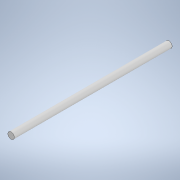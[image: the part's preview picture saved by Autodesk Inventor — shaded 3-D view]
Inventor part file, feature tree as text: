
AUTODESK INVENTOR PART (.ipt)
format: ipt  version: 2021 (Build 250183000, 183)  size: 100,864 bytes
history: native  units: mm
features: sketch x3, extrude x2
ambient origin geometry x8: Origin, YZ Plane, XZ Plane, XY Plane, X Axis, Y Axis, Z Axis, Center Point
bodies: Solid1 (feature_tree)
feature tree (5):
  extrude  "Extrusion1"  Depth=49.5mm TaperAngle=0.0deg
  sketch  "Sketch3"  dims[d7=25.0mm d8=0.0mm d3=0.5mm]
  sketch  "Sketch4"  dims[d4=0.872665mm d5=0.5mm d6=0.872665mm]
  extrude  "Extrusion4"  Depth=25.0mm
  sketch  "Sketch1"  dims[d0=3.0mm d1=49.5mm d2=0.0mm]
